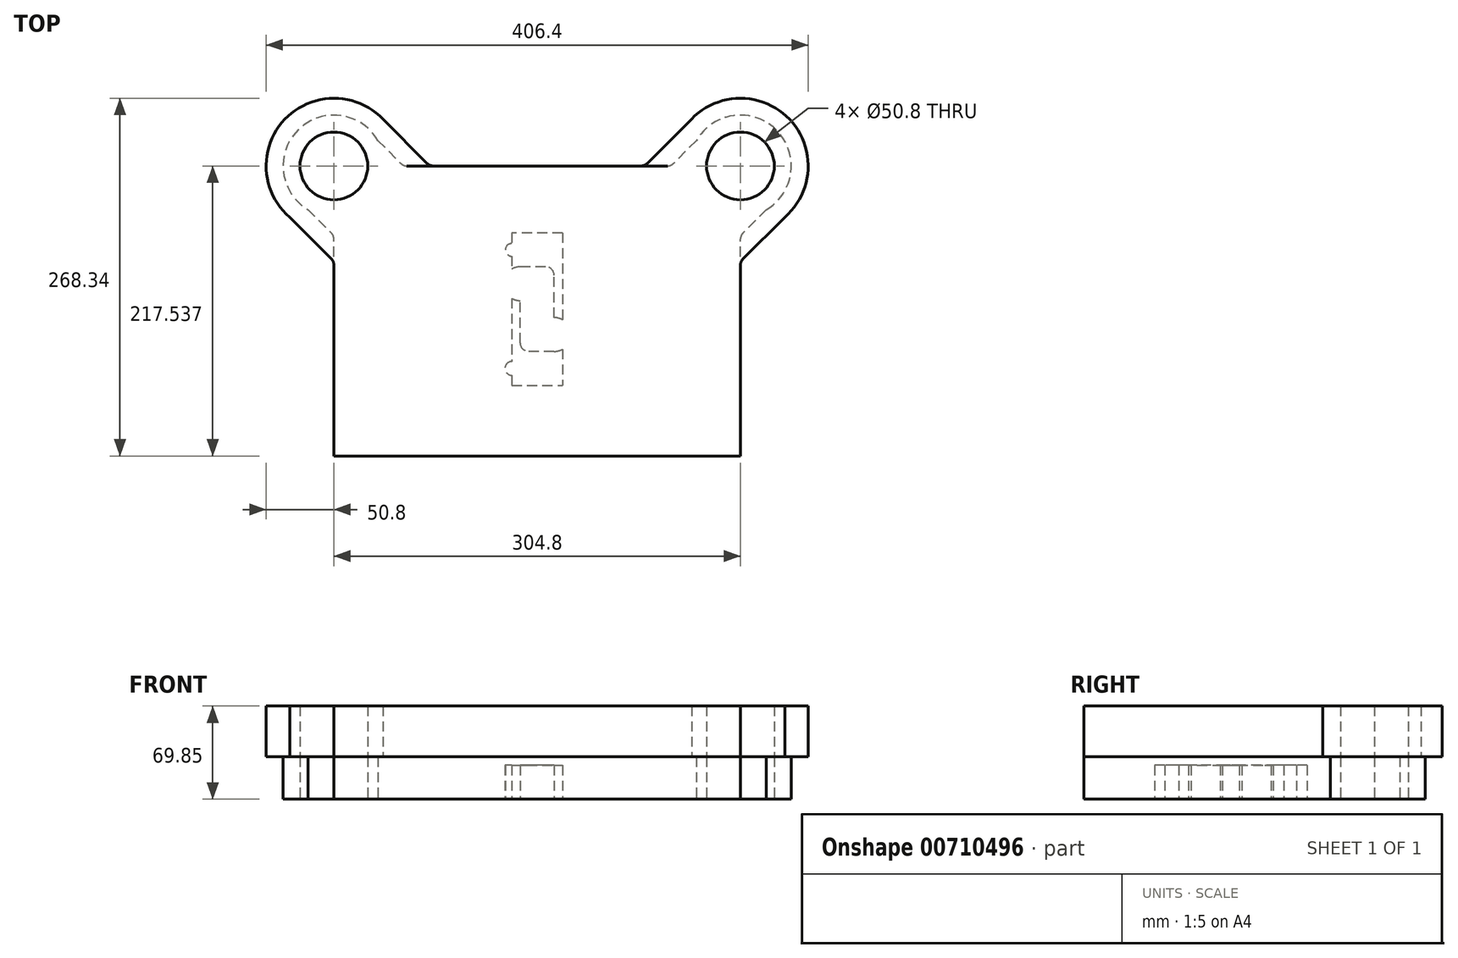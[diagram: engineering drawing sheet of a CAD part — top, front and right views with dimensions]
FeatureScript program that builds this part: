
annotation { "Feature Type Name" : "Feature", "Feature Type Description" : "" }
export const myFeature = defineFeature(function(context is Context, id is Id, definition is map)
    precondition{}
    {
        {
            var Q0;
            Q0=qCreatedBy(makeId("Top.planeOp"),FACE);
            var sketch = newSketch(context, id + "F0", { "sketchPlane" : qUnion([Q0])});
            skLineSegment(sketch, "E0.bottom", {"start": v(-152.4, -108.77) * mm, "end": v(152.4, -108.77) * mm});
            skLineSegment(sketch, "E0.top", {"start": v(-97.72, 108.77) * mm, "end": v(97.72, 108.77) * mm});
            skLineSegment(sketch, "E0.left", {"start": v(-152.4, -108.77) * mm, "end": v(-152.4, 70.67) * mm});
            skLineSegment(sketch, "E0.right", {"start": v(152.4, -108.77) * mm, "end": v(152.4, 53.9) * mm});
            skPoint(sketch, "E0.middle", {"position": v(0, 0) * mm});
            skCircle(sketch, "E1", {"center": v(-152.4, 108.77) * mm, "radius": 38.1 * mm});
            skCircle(sketch, "E2", {"center": v(152.4, 108.77) * mm, "radius": 38.1 * mm});
            skPoint(sketch, "E3", {"position": v(-119.4, 127.82) * mm});
            skPoint(sketch, "E4.MirrorP", {"position": v(119.4, 127.82) * mm});
            skLineSegment(sketch, "E5", {"start": v(-119.4, 127.82) * mm, "end": v(-102.21, 110.63) * mm});
            skLineSegment(sketch, "E6.MirrorCS", {"start": v(119.4, 127.82) * mm, "end": v(102.21, 110.63) * mm});
            skPoint(sketch, "E7.newPointB", {"position": v(100.35, 108.77) * mm});
            skArc(sketch, "E7.filletArc", {"start": v(97.72, 108.77) * mm, "mid": v(100.15, 109.25) * mm, "end": v(102.21, 110.63) * mm});
            skPoint(sketch, "E8.newPointA", {"position": v(-100.35, 108.77) * mm});
            skArc(sketch, "E8.filletArc", {"start": v(-102.21, 110.63) * mm, "mid": v(-100.15, 109.25) * mm, "end": v(-97.72, 108.77) * mm});
            skLineSegment(sketch, "E9", {"start": v(171.9, 76.04) * mm, "end": v(154.26, 58.4) * mm});
            skArc(sketch, "E10.filletArc", {"start": v(154.26, 58.4) * mm, "mid": v(152.88, 56.33) * mm, "end": v(152.4, 53.9) * mm});
            skLineSegment(sketch, "E11.MirrorCS", {"start": v(-171.9, 76.04) * mm, "end": v(-154.26, 58.4) * mm});
            skArc(sketch, "E12.MirrorCS", {"start": v(-154.26, 58.4) * mm, "mid": v(-152.88, 56.33) * mm, "end": v(-152.4, 53.9) * mm});
            skCircle(sketch, "E13", {"center": v(-152.4, 108.77) * mm, "radius": 25.4 * mm});
            skCircle(sketch, "E14", {"center": v(152.4, 108.77) * mm, "radius": 25.4 * mm});
            skSolve(sketch);
        }
        {
            var Q0;
            {var subQ7=sQuery(id+"F0.wireOp",EDGE,"E0.bottom");Q0=makeQuery(id+"F0.imprint","IMPRINT",FACE,{"disambiguationData":[TD([[makeQuery(id+"F0.imprint","IMPRINT",EDGE,{"derivedFrom":subQ7}),1.0]])]});}
            var Q1;
            Q1=makeQuery(id+"F0.imprint","IMPRINT",FACE,{"disambiguationData":[TD([[makeQuery(id+"F0.imprint","IMPRINT",EDGE,{"derivedFrom":sQuery(id+"F0.wireOp",EDGE,"E13")}),-1.0]])]});
            var Q2;
            Q2=makeQuery(id+"F0.imprint","IMPRINT",FACE,{"disambiguationData":[TD([[makeQuery(id+"F0.imprint","IMPRINT",EDGE,{"derivedFrom":sQuery(id+"F0.wireOp",EDGE,"E14")}),-1.0]])]});
            var Q3;
            {var subQ4=sQuery(id+"F0.wireOp",EDGE,"E11.MirrorCS");Q3=makeQuery(id+"F0.imprint","IMPRINT",FACE,{"disambiguationData":[TD([[makeQuery(id+"F0.imprint","IMPRINT",EDGE,{"derivedFrom":subQ4}),1.0]])]});}
            extrude(context, id + "F1", {"entities" : qUnion([Q0, Q1, Q2, Q3]), "depth" : 31.75 * mm, "offsetDistance" : 25.4 * mm});
        }
        {
            var Q0;
            Q0=makeQuery(id+"F1.opExtrude","SWEPT_BODY",BODY,{"disambiguationData":[OSD([sQuery(id+"F0.wireOp",EDGE,"E0.bottom"),sQuery(id+"F0.wireOp",EDGE,"E0.top"),sQuery(id+"F0.wireOp",EDGE,"E0.left"),sQuery(id+"F0.wireOp",EDGE,"E0.right"),sQuery(id+"F0.wireOp",EDGE,"E1"),sQuery(id+"F0.wireOp",EDGE,"E2"),sQuery(id+"F0.wireOp",EDGE,"E5"),sQuery(id+"F0.wireOp",EDGE,"E6.MirrorCS"),sQuery(id+"F0.wireOp",EDGE,"E7.filletArc"),sQuery(id+"F0.wireOp",EDGE,"E8.filletArc"),sQuery(id+"F0.wireOp",EDGE,"E9"),sQuery(id+"F0.wireOp",EDGE,"E10.filletArc"),sQuery(id+"F0.wireOp",EDGE,"E11.MirrorCS"),sQuery(id+"F0.wireOp",EDGE,"E12.MirrorCS"),sQuery(id+"F0.wireOp",EDGE,"E13"),sQuery(id+"F0.wireOp",EDGE,"E14")])]});
            transform(context, id + "F2", {"entities" : qUnion([Q0]), "transformType" : TransformType.TRANSLATION_3D, "dx" : 0 * mm, "dy" : 0 * mm, "dz" : 0 * mm, "makeCopy" : true});
        }
        {
            var Q0;
            Q0=makeQuery(id+"F2.opPattern","COPY",BODY,{"derivedFrom":makeQuery(id+"F1.opExtrude","SWEPT_BODY",BODY,{"disambiguationData":[OSD([sQuery(id+"F0.wireOp",EDGE,"E0.bottom"),sQuery(id+"F0.wireOp",EDGE,"E0.top"),sQuery(id+"F0.wireOp",EDGE,"E0.left"),sQuery(id+"F0.wireOp",EDGE,"E0.right"),sQuery(id+"F0.wireOp",EDGE,"E1"),sQuery(id+"F0.wireOp",EDGE,"E2"),sQuery(id+"F0.wireOp",EDGE,"E5"),sQuery(id+"F0.wireOp",EDGE,"E6.MirrorCS"),sQuery(id+"F0.wireOp",EDGE,"E7.filletArc"),sQuery(id+"F0.wireOp",EDGE,"E8.filletArc"),sQuery(id+"F0.wireOp",EDGE,"E9"),sQuery(id+"F0.wireOp",EDGE,"E10.filletArc"),sQuery(id+"F0.wireOp",EDGE,"E11.MirrorCS"),sQuery(id+"F0.wireOp",EDGE,"E12.MirrorCS"),sQuery(id+"F0.wireOp",EDGE,"E13"),sQuery(id+"F0.wireOp",EDGE,"E14")])]}),"instanceName":"1"});
            deleteBodies(context, id + "F3", {"entities" : qUnion([Q0])});
        }
        {
            var Q0;
            Q0=makeQuery(id+"F1.opExtrude","CAP_FACE",FACE,{"disambiguationData":[OSD([sQuery(id+"F0.wireOp",EDGE,"E0.bottom"),sQuery(id+"F0.wireOp",EDGE,"E0.top"),sQuery(id+"F0.wireOp",EDGE,"E0.left"),sQuery(id+"F0.wireOp",EDGE,"E0.right"),sQuery(id+"F0.wireOp",EDGE,"E1"),sQuery(id+"F0.wireOp",EDGE,"E2"),sQuery(id+"F0.wireOp",EDGE,"E5"),sQuery(id+"F0.wireOp",EDGE,"E6.MirrorCS"),sQuery(id+"F0.wireOp",EDGE,"E7.filletArc"),sQuery(id+"F0.wireOp",EDGE,"E8.filletArc"),sQuery(id+"F0.wireOp",EDGE,"E9"),sQuery(id+"F0.wireOp",EDGE,"E10.filletArc"),sQuery(id+"F0.wireOp",EDGE,"E11.MirrorCS"),sQuery(id+"F0.wireOp",EDGE,"E12.MirrorCS"),sQuery(id+"F0.wireOp",EDGE,"E13"),sQuery(id+"F0.wireOp",EDGE,"E14")])],"isStart":false});
            var sketch = newSketch(context, id + "F4", { "sketchPlane" : qUnion([Q0])});
            skCircle(sketch, "E15", {"center": v(-152.4, 108.77) * mm, "radius": 25.4 * mm});
            skCircle(sketch, "E16", {"center": v(152.4, 108.77) * mm, "radius": 25.4 * mm});
            skLineSegment(sketch, "E17.bottom", {"start": v(152.4, -108.77) * mm, "end": v(-152.4, -108.77) * mm});
            skLineSegment(sketch, "E17.top", {"start": v(77.94, 108.77) * mm, "end": v(-77.94, 108.77) * mm});
            skLineSegment(sketch, "E17.left", {"start": v(152.4, -108.77) * mm, "end": v(152.4, 34.49) * mm});
            skLineSegment(sketch, "E17.right", {"start": v(-152.4, -108.77) * mm, "end": v(-152.4, 34.49) * mm});
            skPoint(sketch, "E17.middle", {"position": v(0, 0) * mm});
            skArc(sketch, "E18", {"start": v(-115.71, 143.9) * mm, "mid": v(-189.24, 143.75) * mm, "end": v(-185.6, 70.31) * mm});
            skArc(sketch, "E19", {"start": v(185.6, 70.31) * mm, "mid": v(189.24, 143.75) * mm, "end": v(115.71, 143.9) * mm});
            skLineSegment(sketch, "E20", {"start": v(-117.26, 145.46) * mm, "end": v(-82.43, 110.63) * mm});
            skArc(sketch, "E21.filletArc", {"start": v(-82.43, 110.63) * mm, "mid": v(-80.37, 109.25) * mm, "end": v(-77.94, 108.77) * mm});
            skLineSegment(sketch, "E22.MirrorCS", {"start": v(117.26, 145.46) * mm, "end": v(82.43, 110.63) * mm});
            skArc(sketch, "E23.MirrorCS", {"start": v(82.43, 110.63) * mm, "mid": v(80.37, 109.25) * mm, "end": v(77.94, 108.77) * mm});
            skLineSegment(sketch, "E24", {"start": v(-190.85, 75.57) * mm, "end": v(-154.26, 38.98) * mm});
            skArc(sketch, "E25.filletArc", {"start": v(-152.4, 34.49) * mm, "mid": v(-152.88, 36.92) * mm, "end": v(-154.26, 38.98) * mm});
            skLineSegment(sketch, "E26.MirrorCS", {"start": v(190.85, 75.57) * mm, "end": v(154.26, 38.98) * mm});
            skArc(sketch, "E27.MirrorCS", {"start": v(152.4, 34.49) * mm, "mid": v(152.88, 36.92) * mm, "end": v(154.26, 38.98) * mm});
            skSolve(sketch);
        }
        {
            var Q0;
            Q0=qSketchRegion(id+"F4",true);
            extrude(context, id + "F5", {"entities" : qUnion([Q0]), "depth" : 38.1 * mm, "offsetDistance" : 25.4 * mm});
        }
        {
            var Q0;
            Q0=qCreatedBy(makeId("Top.planeOp"),FACE);
            var sketch = newSketch(context, id + "F6", { "sketchPlane" : qUnion([Q0])});
            skArc(sketch, "E28.0.0", {"start": v(38.1, 56.96) * mm, "mid": v(37.63, 58.08) * mm, "end": v(36.51, 58.54) * mm});
            skLineSegment(sketch, "E28.0.1", {"start": v(36.51, 58.54) * mm, "end": v(-36.51, 58.54) * mm});
            skArc(sketch, "E28.0.2", {"start": v(-36.51, 58.54) * mm, "mid": v(-37.64, 58.08) * mm, "end": v(-38.1, 56.96) * mm});
            skLineSegment(sketch, "E28.0.3", {"start": v(-38.1, 56.96) * mm, "end": v(-38.1, -54.17) * mm});
            skArc(sketch, "E28.0.4", {"start": v(-38.1, -54.17) * mm, "mid": v(-37.64, -55.3) * mm, "end": v(-36.51, -55.76) * mm});
            skLineSegment(sketch, "E28.0.5", {"start": v(-36.51, -55.76) * mm, "end": v(36.51, -55.76) * mm});
            skArc(sketch, "E28.0.6", {"start": v(36.51, -55.76) * mm, "mid": v(37.63, -55.3) * mm, "end": v(38.1, -54.17) * mm});
            skLineSegment(sketch, "E28.0.7", {"start": v(38.1, -54.17) * mm, "end": v(38.1, 56.96) * mm});
            skLineSegment(sketch, "E29", {"start": v(6.35, 33.14) * mm, "end": v(-12.7, 33.14) * mm});
            skArc(sketch, "E30", {"start": v(-12.7, 33.14) * mm, "mid": v(-25.4, 20.44) * mm, "end": v(-12.7, 7.74) * mm});
            skLineSegment(sketch, "E31", {"start": v(-12.7, -24) * mm, "end": v(-12.7, 7.74) * mm});
            skArc(sketch, "E32", {"start": v(-12.7, -24) * mm, "mid": v(-10.84, -28.5) * mm, "end": v(-6.35, -30.36) * mm});
            skLineSegment(sketch, "E33", {"start": v(12.7, -30.36) * mm, "end": v(-6.35, -30.36) * mm});
            skArc(sketch, "E34", {"start": v(12.7, -30.36) * mm, "mid": v(25.4, -17.66) * mm, "end": v(12.7, -4.96) * mm});
            skLineSegment(sketch, "E35", {"start": v(12.7, -4.96) * mm, "end": v(12.7, 26.8) * mm});
            skArc(sketch, "E36", {"start": v(12.7, 26.8) * mm, "mid": v(10.84, 31.28) * mm, "end": v(6.35, 33.14) * mm});
            skLineSegment(sketch, "E37", {"start": v(38.1, 45.84) * mm, "end": v(-38.1, 45.84) * mm});
            skLineSegment(sketch, "E38", {"start": v(38.1, -43.06) * mm, "end": v(-38.1, -43.06) * mm});
            skLineSegment(sketch, "E39.direction1", {"start": v(-12.7, -55.76) * mm, "end": v(12.7, -55.76) * mm, "construction": true});
            skLineSegment(sketch, "E40", {"start": v(-19.05, 58.54) * mm, "end": v(-19.05, -55.76) * mm});
            skLineSegment(sketch, "E41", {"start": v(19.05, 58.54) * mm, "end": v(19.05, -55.76) * mm});
            skCircle(sketch, "E42", {"center": v(-19.05, 45.84) * mm, "radius": 4.76 * mm});
            skCircle(sketch, "E43", {"center": v(19.05, -43.06) * mm, "radius": 4.76 * mm});
            skCircle(sketch, "E44", {"center": v(19.05, 45.84) * mm, "radius": 5.16 * mm});
            skCircle(sketch, "E45", {"center": v(-19.05, -43.06) * mm, "radius": 5.16 * mm});
            skSolve(sketch);
        }
        {
            var Q0;
            {var subQ0=sQuery(id+"F6.wireOp",EDGE,"E45");var subQ1=sQuery(id+"F6.wireOp",EDGE,"E38");var subQ2=makeQuery(id+"F6.imprint","INTERSECT",VERTEX,{"disambiguationData":[OD(0.0)],"derivedFrom":[subQ1,subQ0]});Q0=makeQuery(id+"F6.imprint","IMPRINT",FACE,{"disambiguationData":[TD([[makeQuery(id+"F6.imprint","IMPRINT",EDGE,{"disambiguationData":[TD([[subQ2,-1.0]])],"derivedFrom":subQ1}),1.0]])]});}
            var Q1;
            {var subQ0=sQuery(id+"F6.wireOp",EDGE,"E40");var subQ1=sQuery(id+"F6.wireOp",EDGE,"E38");var subQ2=makeQuery(id+"F6.imprint","INTERSECT",VERTEX,{"derivedFrom":[subQ1,subQ0]});Q1=makeQuery(id+"F6.imprint","IMPRINT",FACE,{"disambiguationData":[TD([[makeQuery(id+"F6.imprint","IMPRINT",EDGE,{"disambiguationData":[TD([[subQ2,-1.0]])],"derivedFrom":subQ1}),1.0]])]});}
            var Q2;
            {var subQ0=sQuery(id+"F6.wireOp",EDGE,"E40");var subQ1=sQuery(id+"F6.wireOp",EDGE,"E38");var subQ2=makeQuery(id+"F6.imprint","INTERSECT",VERTEX,{"derivedFrom":[subQ1,subQ0]});Q2=makeQuery(id+"F6.imprint","IMPRINT",FACE,{"disambiguationData":[TD([[makeQuery(id+"F6.imprint","IMPRINT",EDGE,{"disambiguationData":[TD([[subQ2,-1.0]])],"derivedFrom":subQ1}),-1.0]])]});}
            var Q3;
            {var subQ0=sQuery(id+"F6.wireOp",EDGE,"E45");var subQ1=sQuery(id+"F6.wireOp",EDGE,"E38");var subQ2=makeQuery(id+"F6.imprint","INTERSECT",VERTEX,{"disambiguationData":[OD(0.0)],"derivedFrom":[subQ1,subQ0]});Q3=makeQuery(id+"F6.imprint","IMPRINT",FACE,{"disambiguationData":[TD([[makeQuery(id+"F6.imprint","IMPRINT",EDGE,{"disambiguationData":[TD([[subQ2,-1.0]])],"derivedFrom":subQ1}),-1.0]])]});}
            var Q4;
            {var subQ0=sQuery(id+"F6.wireOp",EDGE,"E43");var subQ1=sQuery(id+"F6.wireOp",EDGE,"E38");var subQ2=makeQuery(id+"F6.imprint","INTERSECT",VERTEX,{"disambiguationData":[OD(0.0)],"derivedFrom":[subQ1,subQ0]});Q4=makeQuery(id+"F6.imprint","IMPRINT",FACE,{"disambiguationData":[TD([[makeQuery(id+"F6.imprint","IMPRINT",EDGE,{"disambiguationData":[TD([[subQ2,-1.0]])],"derivedFrom":subQ1}),1.0]])]});}
            var Q5;
            {var subQ0=sQuery(id+"F6.wireOp",EDGE,"E41");var subQ1=sQuery(id+"F6.wireOp",EDGE,"E38");var subQ2=makeQuery(id+"F6.imprint","INTERSECT",VERTEX,{"derivedFrom":[subQ1,subQ0]});Q5=makeQuery(id+"F6.imprint","IMPRINT",FACE,{"disambiguationData":[TD([[makeQuery(id+"F6.imprint","IMPRINT",EDGE,{"disambiguationData":[TD([[subQ2,-1.0]])],"derivedFrom":subQ1}),1.0]])]});}
            var Q6;
            {var subQ0=sQuery(id+"F6.wireOp",EDGE,"E41");var subQ1=sQuery(id+"F6.wireOp",EDGE,"E38");var subQ2=makeQuery(id+"F6.imprint","INTERSECT",VERTEX,{"derivedFrom":[subQ1,subQ0]});Q6=makeQuery(id+"F6.imprint","IMPRINT",FACE,{"disambiguationData":[TD([[makeQuery(id+"F6.imprint","IMPRINT",EDGE,{"disambiguationData":[TD([[subQ2,-1.0]])],"derivedFrom":subQ1}),-1.0]])]});}
            var Q7;
            {var subQ0=sQuery(id+"F6.wireOp",EDGE,"E43");var subQ1=sQuery(id+"F6.wireOp",EDGE,"E38");var subQ2=makeQuery(id+"F6.imprint","INTERSECT",VERTEX,{"disambiguationData":[OD(0.0)],"derivedFrom":[subQ1,subQ0]});Q7=makeQuery(id+"F6.imprint","IMPRINT",FACE,{"disambiguationData":[TD([[makeQuery(id+"F6.imprint","IMPRINT",EDGE,{"disambiguationData":[TD([[subQ2,-1.0]])],"derivedFrom":subQ1}),-1.0]])]});}
            var Q8;
            {var subQ0=sQuery(id+"F6.wireOp",EDGE,"E41");var subQ1=sQuery(id+"F6.wireOp",EDGE,"E37");var subQ2=makeQuery(id+"F6.imprint","INTERSECT",VERTEX,{"derivedFrom":[subQ1,subQ0]});Q8=makeQuery(id+"F6.imprint","IMPRINT",FACE,{"disambiguationData":[TD([[makeQuery(id+"F6.imprint","IMPRINT",EDGE,{"disambiguationData":[TD([[subQ2,-1.0]])],"derivedFrom":subQ1}),1.0]])]});}
            var Q9;
            {var subQ0=sQuery(id+"F6.wireOp",EDGE,"E41");var subQ1=sQuery(id+"F6.wireOp",EDGE,"E37");var subQ2=makeQuery(id+"F6.imprint","INTERSECT",VERTEX,{"derivedFrom":[subQ1,subQ0]});Q9=makeQuery(id+"F6.imprint","IMPRINT",FACE,{"disambiguationData":[TD([[makeQuery(id+"F6.imprint","IMPRINT",EDGE,{"disambiguationData":[TD([[subQ2,-1.0]])],"derivedFrom":subQ1}),-1.0]])]});}
            var Q10;
            {var subQ0=sQuery(id+"F6.wireOp",EDGE,"E44");var subQ1=sQuery(id+"F6.wireOp",EDGE,"E37");var subQ2=makeQuery(id+"F6.imprint","INTERSECT",VERTEX,{"disambiguationData":[OD(0.0)],"derivedFrom":[subQ1,subQ0]});Q10=makeQuery(id+"F6.imprint","IMPRINT",FACE,{"disambiguationData":[TD([[makeQuery(id+"F6.imprint","IMPRINT",EDGE,{"disambiguationData":[TD([[subQ2,-1.0]])],"derivedFrom":subQ1}),-1.0]])]});}
            var Q11;
            {var subQ0=sQuery(id+"F6.wireOp",EDGE,"E44");var subQ1=sQuery(id+"F6.wireOp",EDGE,"E37");var subQ2=makeQuery(id+"F6.imprint","INTERSECT",VERTEX,{"disambiguationData":[OD(0.0)],"derivedFrom":[subQ1,subQ0]});Q11=makeQuery(id+"F6.imprint","IMPRINT",FACE,{"disambiguationData":[TD([[makeQuery(id+"F6.imprint","IMPRINT",EDGE,{"disambiguationData":[TD([[subQ2,-1.0]])],"derivedFrom":subQ1}),1.0]])]});}
            var Q12;
            {var subQ0=sQuery(id+"F6.wireOp",EDGE,"E42");var subQ1=sQuery(id+"F6.wireOp",EDGE,"E37");var subQ2=makeQuery(id+"F6.imprint","INTERSECT",VERTEX,{"disambiguationData":[OD(0.0)],"derivedFrom":[subQ1,subQ0]});Q12=makeQuery(id+"F6.imprint","IMPRINT",FACE,{"disambiguationData":[TD([[makeQuery(id+"F6.imprint","IMPRINT",EDGE,{"disambiguationData":[TD([[subQ2,-1.0]])],"derivedFrom":subQ1}),1.0]])]});}
            var Q13;
            {var subQ0=sQuery(id+"F6.wireOp",EDGE,"E42");var subQ1=sQuery(id+"F6.wireOp",EDGE,"E37");var subQ2=makeQuery(id+"F6.imprint","INTERSECT",VERTEX,{"disambiguationData":[OD(0.0)],"derivedFrom":[subQ1,subQ0]});Q13=makeQuery(id+"F6.imprint","IMPRINT",FACE,{"disambiguationData":[TD([[makeQuery(id+"F6.imprint","IMPRINT",EDGE,{"disambiguationData":[TD([[subQ2,-1.0]])],"derivedFrom":subQ1}),-1.0]])]});}
            var Q14;
            {var subQ0=sQuery(id+"F6.wireOp",EDGE,"E40");var subQ1=sQuery(id+"F6.wireOp",EDGE,"E37");var subQ2=makeQuery(id+"F6.imprint","INTERSECT",VERTEX,{"derivedFrom":[subQ1,subQ0]});Q14=makeQuery(id+"F6.imprint","IMPRINT",FACE,{"disambiguationData":[TD([[makeQuery(id+"F6.imprint","IMPRINT",EDGE,{"disambiguationData":[TD([[subQ2,-1.0]])],"derivedFrom":subQ1}),-1.0]])]});}
            var Q15;
            {var subQ0=sQuery(id+"F6.wireOp",EDGE,"E40");var subQ1=sQuery(id+"F6.wireOp",EDGE,"E37");var subQ2=makeQuery(id+"F6.imprint","INTERSECT",VERTEX,{"derivedFrom":[subQ1,subQ0]});Q15=makeQuery(id+"F6.imprint","IMPRINT",FACE,{"disambiguationData":[TD([[makeQuery(id+"F6.imprint","IMPRINT",EDGE,{"disambiguationData":[TD([[subQ2,-1.0]])],"derivedFrom":subQ1}),1.0]])]});}
            extrude(context, id + "F7", {"entities" : qUnion([Q0, Q1, Q2, Q3, Q4, Q5, Q6, Q7, Q8, Q9, Q10, Q11, Q12, Q13, Q14, Q15]), "operationType" : NewBodyOperationType.REMOVE, "oppositeDirection" : true, "depth" : -25.4 * mm, "offsetDistance" : 25.4 * mm});
        }
    });
